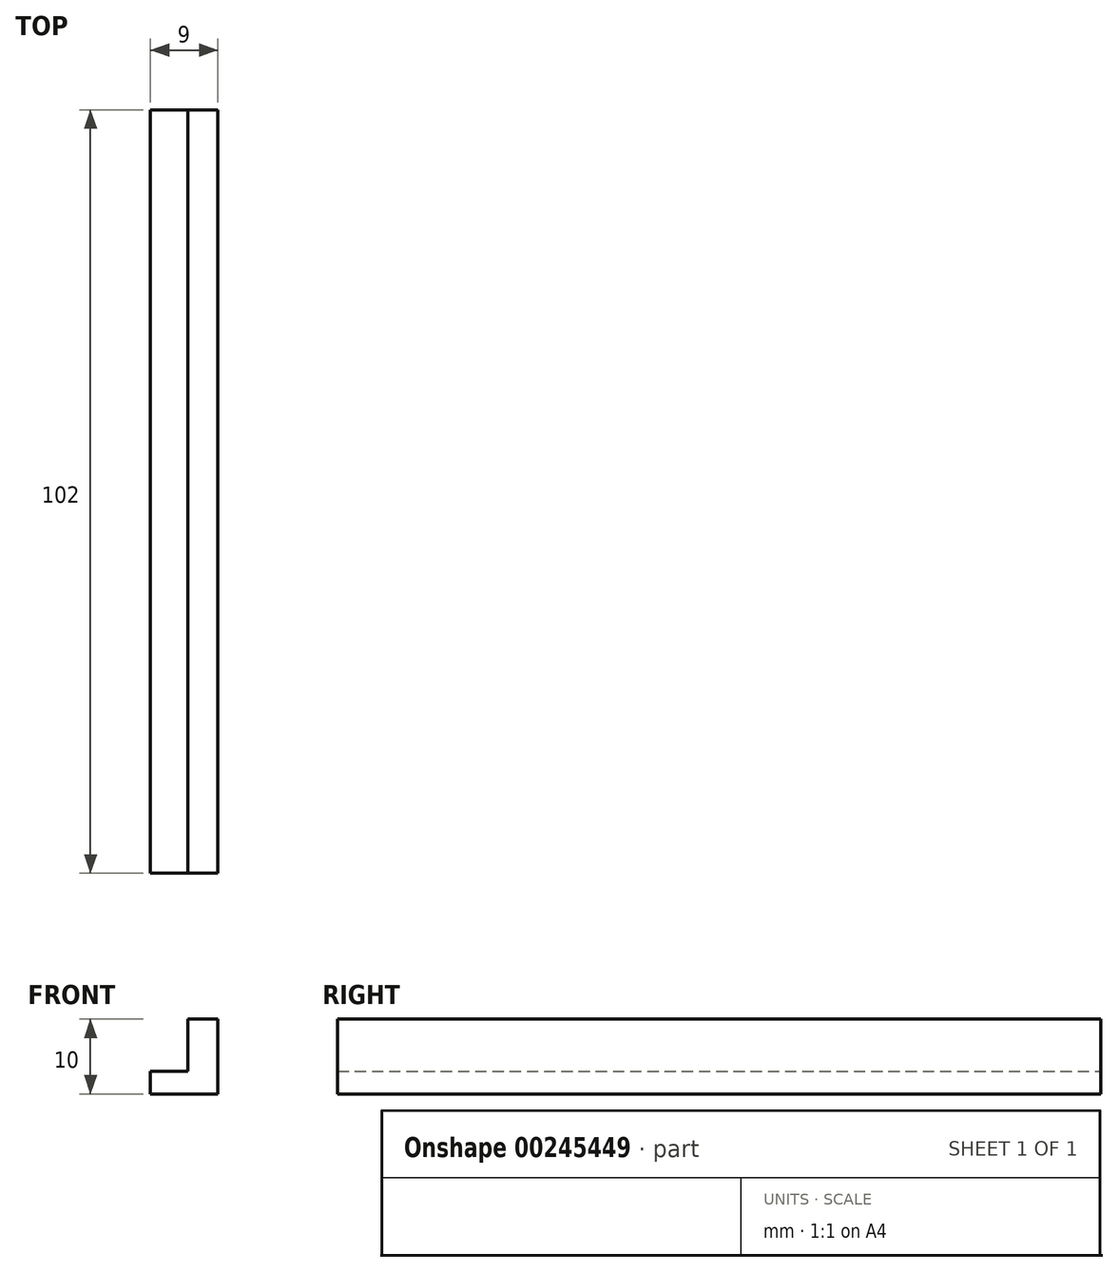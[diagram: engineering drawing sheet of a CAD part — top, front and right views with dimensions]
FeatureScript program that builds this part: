
annotation { "Feature Type Name" : "Feature", "Feature Type Description" : "" }
export const myFeature = defineFeature(function(context is Context, id is Id, definition is map)
    precondition{}
    {
        {
            var Q0;
            Q0=qCreatedBy(makeId("Front.planeOp"),FACE);
            var sketch = newSketch(context, id + "F0", { "sketchPlane" : qUnion([Q0])});
            skLineSegment(sketch, "E0", {"start": v(0, 0) * mm, "end": v(0, 3) * mm});
            skLineSegment(sketch, "E1", {"start": v(0, 3) * mm, "end": v(5, 3) * mm});
            skLineSegment(sketch, "E2", {"start": v(5, 3) * mm, "end": v(5, 10) * mm});
            skLineSegment(sketch, "E3", {"start": v(5, 10) * mm, "end": v(9, 10) * mm});
            skLineSegment(sketch, "E4", {"start": v(9, 10) * mm, "end": v(9, 0) * mm});
            skLineSegment(sketch, "E5", {"start": v(9, 0) * mm, "end": v(0, 0) * mm});
            skSolve(sketch);
        }
        {
            var Q0;
            Q0=qSketchRegion(id+"F0",true);
            extrude(context, id + "F1", {"entities" : qUnion([Q0]), "depth" : (110 - 8) * mm});
        }
    });
